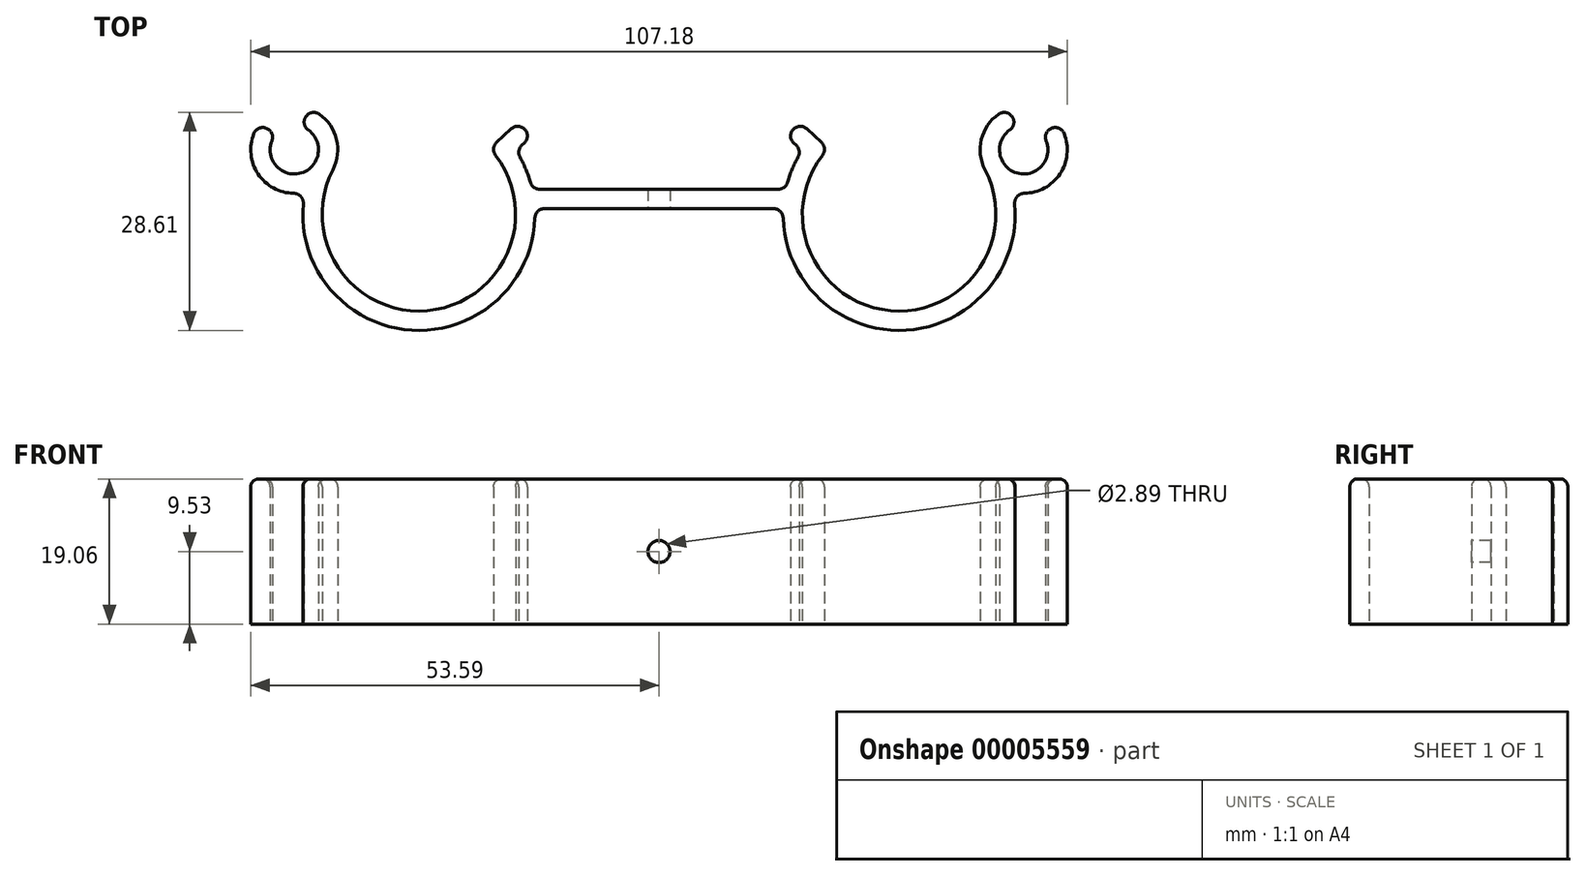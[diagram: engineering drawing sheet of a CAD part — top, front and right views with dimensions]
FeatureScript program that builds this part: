
annotation { "Feature Type Name" : "Feature", "Feature Type Description" : "" }
export const myFeature = defineFeature(function(context is Context, id is Id, definition is map)
    precondition{}
    {
        {
            var Q0;
            Q0=qCreatedBy(makeId("Top.planeOp"),FACE);
            var sketch = newSketch(context, id + "F0", { "sketchPlane" : qUnion([Q0])});
            skArc(sketch, "E0", {"start": v(-42.8, 5.84) * mm, "mid": v(-30.4, -12.65) * mm, "end": v(-21.45, 7.74) * mm});
            skLineSegment(sketch, "E1", {"start": v(-15.66, 3.28) * mm, "end": v(0, 3.28) * mm});
            skLineSegment(sketch, "E2", {"start": v(0, 0) * mm, "end": v(0, 6.96) * mm, "construction": true});
            skLineSegment(sketch, "E3", {"start": v(-31.52, 0) * mm, "end": v(-15.67, 14.66) * mm, "construction": true});
            skLineSegment(sketch, "E4", {"start": v(-31.52, 0) * mm, "end": v(-45.2, 14.79) * mm, "construction": true});
            skLineSegment(sketch, "E5", {"start": v(-21.3, 9.45) * mm, "end": v(-19.4, 11.2) * mm});
            skLineSegment(sketch, "E6.2", {"start": v(-18, 9.03) * mm, "end": v(-17.68, 9.34) * mm});
            skLineSegment(sketch, "E7", {"start": v(-43.65, 12.36) * mm, "end": v(-43.65, 12.36) * mm});
            skLineSegment(sketch, "E8", {"start": v(-17.6, 11.13) * mm, "end": v(-17.6, 11.13) * mm});
            skLineSegment(sketch, "E9.0", {"start": v(-15.02, 0.74) * mm, "end": v(0, 0.74) * mm});
            skArc(sketch, "E10.trimOffspring", {"start": v(-16.88, 4.2) * mm, "mid": v(-17.47, 5.88) * mm, "end": v(-18.25, 7.48) * mm});
            skPoint(sketch, "E11.visualSharp", {"position": v(-43.6, 13.06) * mm});
            skPoint(sketch, "E12.visualSharp", {"position": v(-40.14, 9.32) * mm});
            skPoint(sketch, "E13.visualSharp", {"position": v(-22.2, 8.62) * mm});
            skArc(sketch, "E13.filletArc", {"start": v(-21.3, 9.45) * mm, "mid": v(-21.7, 8.62) * mm, "end": v(-21.45, 7.74) * mm});
            skPoint(sketch, "E14.visualSharp", {"position": v(-18.47, 12.07) * mm});
            skArc(sketch, "E14.filletArc", {"start": v(-17.6, 11.13) * mm, "mid": v(-18.5, 11.54) * mm, "end": v(-19.4, 11.2) * mm});
            skPoint(sketch, "E15.visualSharp", {"position": v(-16.75, 10.2) * mm});
            skArc(sketch, "E15.filletArc", {"start": v(-17.68, 9.34) * mm, "mid": v(-17.27, 10.22) * mm, "end": v(-17.6, 11.13) * mm});
            skPoint(sketch, "E16.visualSharp", {"position": v(-18.77, 8.33) * mm});
            skArc(sketch, "E16.filletArc", {"start": v(-18, 9.03) * mm, "mid": v(-18.4, 8.3) * mm, "end": v(-18.25, 7.48) * mm});
            skPoint(sketch, "E17.visualSharp", {"position": v(-16.65, 3.28) * mm});
            skArc(sketch, "E17.filletArc", {"start": v(-16.88, 4.2) * mm, "mid": v(-16.42, 3.53) * mm, "end": v(-15.66, 3.28) * mm});
            skPoint(sketch, "E18.visualSharp", {"position": v(-16.31, 0.74) * mm});
            skArc(sketch, "E19", {"start": v(-50.82, 9.64) * mm, "mid": v(-46.97, 5.42) * mm, "end": v(-46.05, 11.06) * mm});
            skArc(sketch, "E20.0", {"start": v(-42.8, 5.84) * mm, "mid": v(-42.32, 9.82) * mm, "end": v(-44.59, 13.14) * mm});
            skArc(sketch, "E21.trimOffspring", {"start": v(-46.7, 1.36) * mm, "mid": v(-32.45, -15.21) * mm, "end": v(-16.29, -0.5) * mm});
            skLineSegment(sketch, "E22", {"start": v(-53.58, 12.98) * mm, "end": v(-47.88, 8.46) * mm, "construction": true});
            skLineSegment(sketch, "E23", {"start": v(-47.88, 8.46) * mm, "end": v(-45.33, 16.05) * mm, "construction": true});
            skArc(sketch, "E24.trimOffspring", {"start": v(-53.18, 10.58) * mm, "mid": v(-52.63, 5.29) * mm, "end": v(-47.95, 2.75) * mm});
            skLineSegment(sketch, "E25", {"start": v(-51.21, 11.1) * mm, "end": v(-51.21, 11.1) * mm});
            skLineSegment(sketch, "E26", {"start": v(-46.52, 12.5) * mm, "end": v(-46.52, 12.5) * mm});
            skPoint(sketch, "E27.visualSharp", {"position": v(-52.36, 12.01) * mm});
            skArc(sketch, "E27.filletArc", {"start": v(-51.21, 11.1) * mm, "mid": v(-52.33, 11.34) * mm, "end": v(-53.18, 10.58) * mm});
            skPoint(sketch, "E28.visualSharp", {"position": v(-50.36, 10.43) * mm});
            skArc(sketch, "E28.filletArc", {"start": v(-50.82, 9.64) * mm, "mid": v(-50.78, 10.44) * mm, "end": v(-51.21, 11.1) * mm});
            skPoint(sketch, "E29.visualSharp", {"position": v(-46.87, 11.47) * mm});
            skArc(sketch, "E29.filletArc", {"start": v(-46.52, 12.5) * mm, "mid": v(-46.52, 11.7) * mm, "end": v(-46.05, 11.06) * mm});
            skPoint(sketch, "E30.visualSharp", {"position": v(-46.06, 13.88) * mm});
            skArc(sketch, "E30.filletArc", {"start": v(-44.59, 13.14) * mm, "mid": v(-45.71, 13.3) * mm, "end": v(-46.52, 12.5) * mm});
            skPoint(sketch, "E31.visualSharp", {"position": v(-46.48, 2.92) * mm});
            skArc(sketch, "E31.filletArc", {"start": v(-46.7, 1.36) * mm, "mid": v(-47.02, 2.33) * mm, "end": v(-47.95, 2.75) * mm});
            skPoint(sketch, "E32.visualSharp", {"position": v(-16.3, 0.74) * mm});
            skArc(sketch, "E32.filletArc", {"start": v(-15.02, 0.74) * mm, "mid": v(-15.9, 0.38) * mm, "end": v(-16.29, -0.5) * mm});
            skArc(sketch, "E33.0.MirrorCS", {"start": v(51.21, 11.1) * mm, "mid": v(52.33, 11.34) * mm, "end": v(53.18, 10.58) * mm});
            skArc(sketch, "E33.1.MirrorCS", {"start": v(16.88, 4.2) * mm, "mid": v(16.42, 3.53) * mm, "end": v(15.66, 3.28) * mm});
            skArc(sketch, "E33.2.MirrorCS", {"start": v(50.82, 9.64) * mm, "mid": v(50.78, 10.44) * mm, "end": v(51.21, 11.1) * mm});
            skArc(sketch, "E33.3.MirrorCS", {"start": v(17.6, 11.13) * mm, "mid": v(18.5, 11.54) * mm, "end": v(19.4, 11.2) * mm});
            skArc(sketch, "E33.4.MirrorCS", {"start": v(18, 9.03) * mm, "mid": v(18.4, 8.3) * mm, "end": v(18.25, 7.48) * mm});
            skArc(sketch, "E33.5.MirrorCS", {"start": v(21.3, 9.45) * mm, "mid": v(21.7, 8.62) * mm, "end": v(21.45, 7.74) * mm});
            skLineSegment(sketch, "E33.6.MirrorCS", {"start": v(18, 9.03) * mm, "end": v(17.68, 9.34) * mm});
            skArc(sketch, "E33.7.MirrorCS", {"start": v(44.59, 13.14) * mm, "mid": v(45.71, 13.3) * mm, "end": v(46.52, 12.5) * mm});
            skArc(sketch, "E33.8.MirrorCS", {"start": v(46.52, 12.5) * mm, "mid": v(46.52, 11.7) * mm, "end": v(46.05, 11.06) * mm});
            skArc(sketch, "E33.9.MirrorCS", {"start": v(46.7, 1.36) * mm, "mid": v(47.02, 2.33) * mm, "end": v(47.95, 2.75) * mm});
            skArc(sketch, "E33.10.MirrorCS", {"start": v(17.68, 9.34) * mm, "mid": v(17.27, 10.22) * mm, "end": v(17.6, 11.13) * mm});
            skLineSegment(sketch, "E33.11.MirrorCS", {"start": v(21.3, 9.45) * mm, "end": v(19.4, 11.2) * mm});
            skArc(sketch, "E33.12.MirrorCS", {"start": v(15.02, 0.74) * mm, "mid": v(15.9, 0.38) * mm, "end": v(16.29, -0.5) * mm});
            skPoint(sketch, "E33.13.MirrorP", {"position": v(16.31, 0.74) * mm});
            skLineSegment(sketch, "E33.14.MirrorCS", {"start": v(53.58, 12.98) * mm, "end": v(47.88, 8.46) * mm, "construction": true});
            skPoint(sketch, "E33.15.MirrorP", {"position": v(46.06, 13.88) * mm});
            skArc(sketch, "E33.16.MirrorCS", {"start": v(16.88, 4.2) * mm, "mid": v(17.47, 5.88) * mm, "end": v(18.25, 7.48) * mm});
            skPoint(sketch, "E33.17.MirrorP", {"position": v(18.77, 8.33) * mm});
            skPoint(sketch, "E33.18.MirrorP", {"position": v(52.36, 12.01) * mm});
            skArc(sketch, "E33.19.MirrorCS", {"start": v(46.7, 1.36) * mm, "mid": v(32.45, -15.21) * mm, "end": v(16.29, -0.5) * mm});
            skPoint(sketch, "E33.20.MirrorP", {"position": v(50.36, 10.43) * mm});
            skLineSegment(sketch, "E33.21.MirrorCS", {"start": v(47.88, 8.46) * mm, "end": v(45.33, 16.05) * mm, "construction": true});
            skPoint(sketch, "E33.22.MirrorP", {"position": v(43.6, 13.06) * mm});
            skPoint(sketch, "E33.23.MirrorP", {"position": v(40.14, 9.32) * mm});
            skArc(sketch, "E33.24.MirrorCS", {"start": v(42.8, 5.84) * mm, "mid": v(42.32, 9.82) * mm, "end": v(44.59, 13.14) * mm});
            skArc(sketch, "E33.25.MirrorCS", {"start": v(53.18, 10.58) * mm, "mid": v(52.63, 5.29) * mm, "end": v(47.95, 2.75) * mm});
            skLineSegment(sketch, "E33.26.MirrorCS", {"start": v(51.21, 11.1) * mm, "end": v(51.21, 11.1) * mm});
            skPoint(sketch, "E33.27.MirrorP", {"position": v(46.48, 2.92) * mm});
            skArc(sketch, "E33.28.MirrorCS", {"start": v(50.82, 9.64) * mm, "mid": v(46.97, 5.42) * mm, "end": v(46.05, 11.06) * mm});
            skPoint(sketch, "E33.29.MirrorP", {"position": v(16.3, 0.74) * mm});
            skPoint(sketch, "E33.30.MirrorP", {"position": v(16.75, 10.2) * mm});
            skPoint(sketch, "E33.31.MirrorP", {"position": v(18.47, 12.07) * mm});
            skLineSegment(sketch, "E33.32.MirrorCS", {"start": v(15.02, 0.74) * mm, "end": v(0, 0.74) * mm});
            skLineSegment(sketch, "E33.33.MirrorCS", {"start": v(15.66, 3.28) * mm, "end": v(0, 3.28) * mm});
            skLineSegment(sketch, "E33.34.MirrorCS", {"start": v(31.52, 0) * mm, "end": v(45.2, 14.79) * mm, "construction": true});
            skLineSegment(sketch, "E33.35.MirrorCS", {"start": v(31.52, 0) * mm, "end": v(15.67, 14.66) * mm, "construction": true});
            skArc(sketch, "E33.36.MirrorCS", {"start": v(42.8, 5.84) * mm, "mid": v(30.4, -12.65) * mm, "end": v(21.45, 7.74) * mm});
            skLineSegment(sketch, "E33.37.MirrorCS", {"start": v(17.6, 11.13) * mm, "end": v(17.6, 11.13) * mm});
            skLineSegment(sketch, "E33.38.MirrorCS", {"start": v(46.52, 12.5) * mm, "end": v(46.52, 12.5) * mm});
            skPoint(sketch, "E33.39.MirrorP", {"position": v(16.65, 3.28) * mm});
            skLineSegment(sketch, "E33.40.MirrorCS", {"start": v(43.65, 12.36) * mm, "end": v(43.65, 12.36) * mm});
            skPoint(sketch, "E33.41.MirrorP", {"position": v(46.87, 11.47) * mm});
            skPoint(sketch, "E33.42.MirrorP", {"position": v(22.2, 8.62) * mm});
            skSolve(sketch);
        }
        {
            var Q0;
            Q0 = qSketchRegion(id + "F0", true);
            extrude(context, id + "F1", {"entities" : qUnion([Q0]), "endBound" : BoundingType.SYMMETRIC, "depth" : 19.05 * mm});
        }
        {
            var Q0;
            Q0=makeQuery(id+"F1.opExtrude","SWEPT_FACE",FACE,{"disambiguationData":[OSD([sQuery(id+"F0.wireOp",EDGE,"E9.0"),sQuery(id+"F0.wireOp",EDGE,"d65fd0c4-e5de-48c2-89a7-0995ba587415.4.MirrorCS")])]});
            var sketch = newSketch(context, id + "F2", { "sketchPlane" : qUnion([Q0])});
            skCircle(sketch, "E34", {"center": v(0, 0) * mm, "radius": 1.44 * mm});
            skSolve(sketch);
        }
        {
            var Q0;
            Q0 = qSketchRegion(id + "F2", true);
            extrude(context, id + "F3", {"entities" : qUnion([Q0]), "operationType" : NewBodyOperationType.REMOVE, "endBound" : BoundingType.THROUGH_ALL, "oppositeDirection" : true, "depth" : 25.4 * mm});
        }
        {
            var Q0;
            Q0=makeQuery(id+"F1.opExtrude","CAP_FACE",FACE,{"disambiguationData":[OSD([sQuery(id+"F0.wireOp",EDGE,"E0"),sQuery(id+"F0.wireOp",EDGE,"E1"),sQuery(id+"F0.wireOp",EDGE,"E5"),sQuery(id+"F0.wireOp",EDGE,"E6.2"),sQuery(id+"F0.wireOp",EDGE,"E9.0"),sQuery(id+"F0.wireOp",EDGE,"E10.trimOffspring"),sQuery(id+"F0.wireOp",EDGE,"E13.filletArc"),sQuery(id+"F0.wireOp",EDGE,"E14.filletArc"),sQuery(id+"F0.wireOp",EDGE,"E15.filletArc"),sQuery(id+"F0.wireOp",EDGE,"E16.filletArc"),sQuery(id+"F0.wireOp",EDGE,"E17.filletArc"),sQuery(id+"F0.wireOp",EDGE,"E18.filletArc"),sQuery(id+"F0.wireOp",EDGE,"E19"),sQuery(id+"F0.wireOp",EDGE,"E20.0"),sQuery(id+"F0.wireOp",EDGE,"E21.trimOffspring"),sQuery(id+"F0.wireOp",EDGE,"E24.trimOffspring"),sQuery(id+"F0.wireOp",EDGE,"E27.filletArc"),sQuery(id+"F0.wireOp",EDGE,"E28.filletArc"),sQuery(id+"F0.wireOp",EDGE,"E29.filletArc"),sQuery(id+"F0.wireOp",EDGE,"E30.filletArc"),sQuery(id+"F0.wireOp",EDGE,"E31.filletArc"),sQuery(id+"F0.wireOp",EDGE,"158a7255-d7e7-4427-8df4-94f67b1b1005.0.MirrorCS"),sQuery(id+"F0.wireOp",EDGE,"158a7255-d7e7-4427-8df4-94f67b1b1005.1.MirrorCS"),sQuery(id+"F0.wireOp",EDGE,"158a7255-d7e7-4427-8df4-94f67b1b1005.2.MirrorCS"),sQuery(id+"F0.wireOp",EDGE,"158a7255-d7e7-4427-8df4-94f67b1b1005.3.MirrorCS"),sQuery(id+"F0.wireOp",EDGE,"158a7255-d7e7-4427-8df4-94f67b1b1005.4.MirrorCS"),sQuery(id+"F0.wireOp",EDGE,"158a7255-d7e7-4427-8df4-94f67b1b1005.5.MirrorCS"),sQuery(id+"F0.wireOp",EDGE,"158a7255-d7e7-4427-8df4-94f67b1b1005.6.MirrorCS"),sQuery(id+"F0.wireOp",EDGE,"158a7255-d7e7-4427-8df4-94f67b1b1005.7.MirrorCS"),sQuery(id+"F0.wireOp",EDGE,"158a7255-d7e7-4427-8df4-94f67b1b1005.8.MirrorCS"),sQuery(id+"F0.wireOp",EDGE,"158a7255-d7e7-4427-8df4-94f67b1b1005.9.MirrorCS"),sQuery(id+"F0.wireOp",EDGE,"158a7255-d7e7-4427-8df4-94f67b1b1005.10.MirrorCS"),sQuery(id+"F0.wireOp",EDGE,"158a7255-d7e7-4427-8df4-94f67b1b1005.11.MirrorCS"),sQuery(id+"F0.wireOp",EDGE,"158a7255-d7e7-4427-8df4-94f67b1b1005.18.MirrorCS"),sQuery(id+"F0.wireOp",EDGE,"158a7255-d7e7-4427-8df4-94f67b1b1005.20.MirrorCS"),sQuery(id+"F0.wireOp",EDGE,"158a7255-d7e7-4427-8df4-94f67b1b1005.22.MirrorCS"),sQuery(id+"F0.wireOp",EDGE,"158a7255-d7e7-4427-8df4-94f67b1b1005.24.MirrorCS"),sQuery(id+"F0.wireOp",EDGE,"158a7255-d7e7-4427-8df4-94f67b1b1005.25.MirrorCS"),sQuery(id+"F0.wireOp",EDGE,"158a7255-d7e7-4427-8df4-94f67b1b1005.27.MirrorCS"),sQuery(id+"F0.wireOp",EDGE,"158a7255-d7e7-4427-8df4-94f67b1b1005.32.MirrorCS"),sQuery(id+"F0.wireOp",EDGE,"158a7255-d7e7-4427-8df4-94f67b1b1005.34.MirrorCS"),sQuery(id+"F0.wireOp",EDGE,"158a7255-d7e7-4427-8df4-94f67b1b1005.39.MirrorCS")])],"isStart":false});
            fillet(context, id + "F4", {"entities" : qUnion([Q0]), "radius" : 1.02 * mm, "tangentPropagation" : true, "allowEdgeOverflow" : false});
        }
    });
